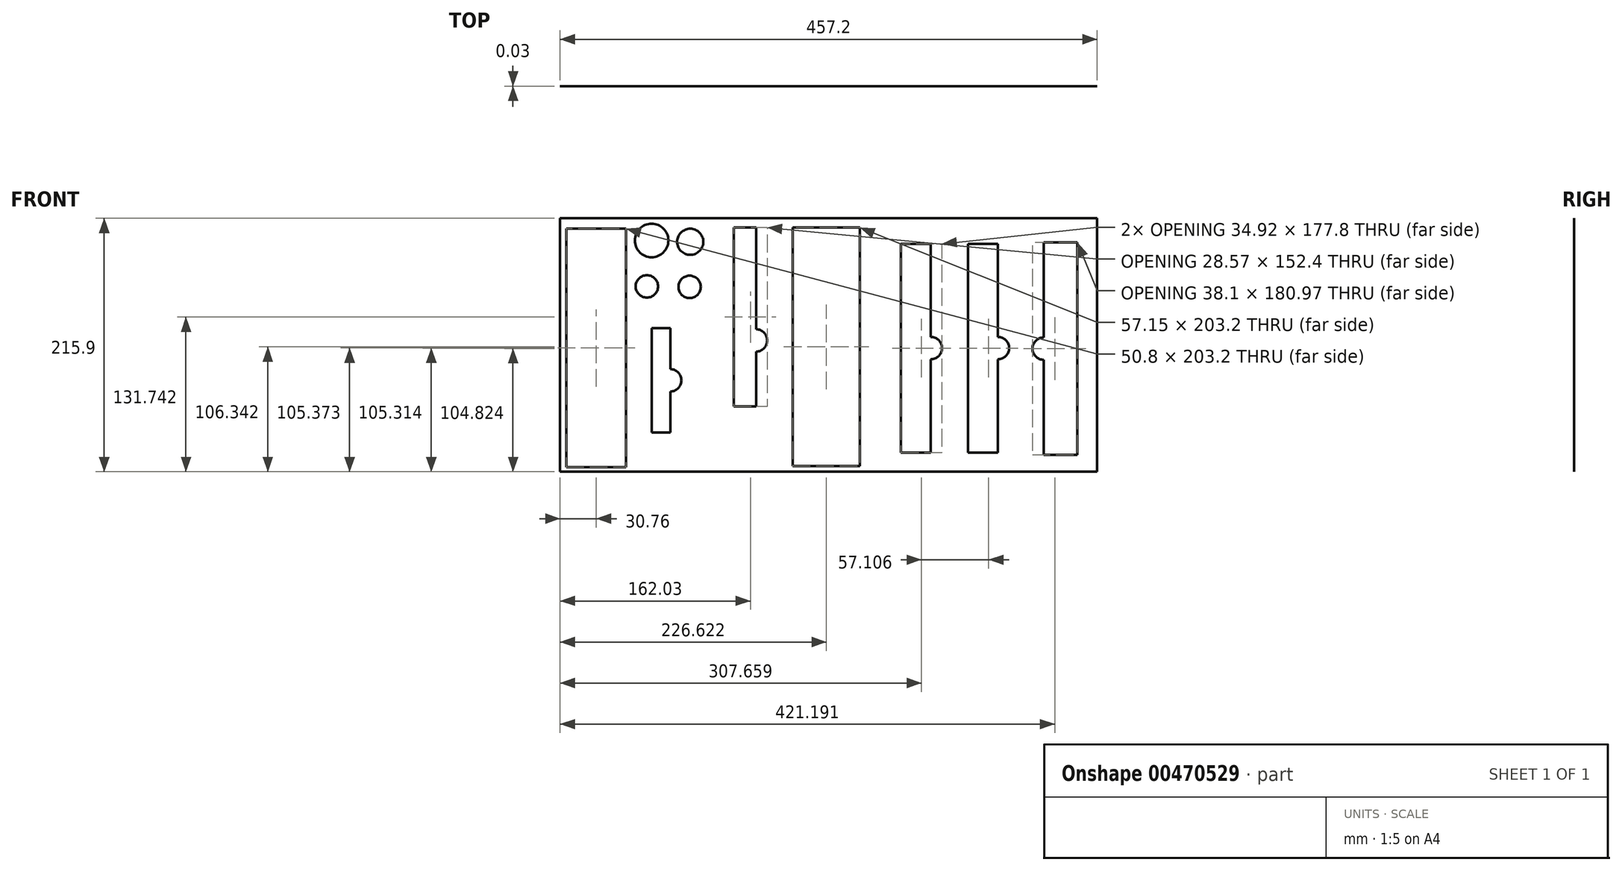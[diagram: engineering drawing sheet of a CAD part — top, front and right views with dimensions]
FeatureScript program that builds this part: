
annotation { "Feature Type Name" : "Feature", "Feature Type Description" : "" }
export const myFeature = defineFeature(function(context is Context, id is Id, definition is map)
    precondition{}
    {
        {
            var Q0;
            Q0=qCreatedBy(makeId("Front.planeOp"),FACE);
            var sketch = newSketch(context, id + "F0", { "sketchPlane" : qUnion([Q0])});
            skLineSegment(sketch, "E0.bottom", {"start": v(-194.02, 115.7) * mm, "end": v(263.18, 115.7) * mm});
            skLineSegment(sketch, "E0.top", {"start": v(-194.02, -100.2) * mm, "end": v(263.18, -100.2) * mm});
            skLineSegment(sketch, "E0.right", {"start": v(263.18, 115.7) * mm, "end": v(263.18, -100.2) * mm});
            skLineSegment(sketch, "E1", {"start": v(-194.02, 115.7) * mm, "end": v(-194.02, -100.2) * mm});
            skSolve(sketch);
        }
        {
            var Q0;
            Q0=makeQuery(id+"F0.imprint","IMPRINT",FACE,{"disambiguationData":[TD([[makeQuery(id+"F0.imprint","IMPRINT",EDGE,{"derivedFrom":sQuery(id+"F0.wireOp",EDGE,"E0.bottom")}),-1.0]])]});
            extrude(context, id + "F1", {"entities" : qUnion([Q0]), "depth" : 3 / 101.6 * mm});
        }
        {
            var Q0;
            Q0=makeQuery(id+"F1.opExtrude","CAP_FACE",FACE,{"disambiguationData":[OSD([sQuery(id+"F0.wireOp",EDGE,"E0.bottom"),sQuery(id+"F0.wireOp",EDGE,"E0.top"),sQuery(id+"F0.wireOp",EDGE,"E0.right"),sQuery(id+"F0.wireOp",EDGE,"E1")])],"isStart":false});
            var sketch = newSketch(context, id + "F2", { "sketchPlane" : qUnion([Q0])});
            skLineSegment(sketch, "E2.bottom", {"start": v(-188.66, 106.77) * mm, "end": v(-137.86, 106.77) * mm});
            skLineSegment(sketch, "E2.top", {"start": v(-188.66, -96.43) * mm, "end": v(-137.86, -96.43) * mm});
            skLineSegment(sketch, "E2.left", {"start": v(-188.66, 106.77) * mm, "end": v(-188.66, -96.43) * mm});
            skLineSegment(sketch, "E2.right", {"start": v(-137.86, 106.77) * mm, "end": v(-137.86, -96.43) * mm});
            skCircle(sketch, "E3", {"center": v(-120.18, 57.68) * mm, "radius": 9.53 * mm});
            skCircle(sketch, "E4", {"center": v(-83.23, 95.66) * mm, "radius": 11.11 * mm});
            skCircle(sketch, "E5", {"center": v(-116.13, 96.76) * mm, "radius": 14.29 * mm});
            skCircle(sketch, "E6", {"center": v(-83.78, 57.22) * mm, "radius": 9.53 * mm});
            skLineSegment(sketch, "E7.bottom", {"start": v(-46.28, 107.74) * mm, "end": v(-27.23, 107.74) * mm});
            skLineSegment(sketch, "E7.top", {"start": v(-46.28, -44.66) * mm, "end": v(-27.23, -44.66) * mm});
            skLineSegment(sketch, "E7.left", {"start": v(-46.28, 107.74) * mm, "end": v(-46.28, -44.66) * mm});
            skLineSegment(sketch, "E7.right", {"start": v(-27.23, 107.74) * mm, "end": v(-27.23, -44.66) * mm});
            skLineSegment(sketch, "E8.bottom", {"start": v(4.03, 107.74) * mm, "end": v(61.18, 107.74) * mm});
            skLineSegment(sketch, "E8.top", {"start": v(4.03, -95.46) * mm, "end": v(61.18, -95.46) * mm});
            skLineSegment(sketch, "E8.left", {"start": v(4.03, 107.74) * mm, "end": v(4.03, -95.46) * mm});
            skLineSegment(sketch, "E8.right", {"start": v(61.18, 107.74) * mm, "end": v(61.18, -95.46) * mm});
            skLineSegment(sketch, "E9.bottom", {"start": v(96.18, 94.01) * mm, "end": v(121.58, 94.01) * mm});
            skLineSegment(sketch, "E9.top", {"start": v(96.18, -83.79) * mm, "end": v(121.58, -83.79) * mm});
            skLineSegment(sketch, "E9.left", {"start": v(96.18, 94.01) * mm, "end": v(96.18, -83.79) * mm});
            skLineSegment(sketch, "E9.right", {"start": v(121.58, 94.01) * mm, "end": v(121.58, -83.79) * mm});
            skLineSegment(sketch, "E10.bottom", {"start": v(153.28, 94.01) * mm, "end": v(178.68, 94.01) * mm});
            skLineSegment(sketch, "E10.top", {"start": v(153.28, -83.79) * mm, "end": v(178.68, -83.79) * mm});
            skLineSegment(sketch, "E10.left", {"start": v(153.28, 94.01) * mm, "end": v(153.28, -83.79) * mm});
            skLineSegment(sketch, "E10.right", {"start": v(178.68, 94.01) * mm, "end": v(178.68, -83.79) * mm});
            skLineSegment(sketch, "E11.bottom", {"start": v(217.65, 95.11) * mm, "end": v(246.22, 95.11) * mm});
            skLineSegment(sketch, "E11.top", {"start": v(217.65, -85.86) * mm, "end": v(246.22, -85.86) * mm});
            skLineSegment(sketch, "E11.left", {"start": v(217.65, 95.11) * mm, "end": v(217.65, -85.86) * mm});
            skLineSegment(sketch, "E11.right", {"start": v(246.22, 95.11) * mm, "end": v(246.22, -85.86) * mm});
            skLineSegment(sketch, "E12.bottom", {"start": v(-116.13, 22.08) * mm, "end": v(-100.26, 22.08) * mm});
            skLineSegment(sketch, "E12.top", {"start": v(-116.13, -66.82) * mm, "end": v(-100.26, -66.82) * mm});
            skLineSegment(sketch, "E12.left", {"start": v(-116.13, 22.08) * mm, "end": v(-116.13, -66.82) * mm});
            skLineSegment(sketch, "E12.right", {"start": v(-100.26, 22.08) * mm, "end": v(-100.26, -66.82) * mm});
            skSolve(sketch);
        }
        {
            var Q0;
            Q0=makeQuery(id+"F2.imprint","IMPRINT",FACE,{"disambiguationData":[TD([[makeQuery(id+"F2.imprint","IMPRINT",EDGE,{"derivedFrom":sQuery(id+"F2.wireOp",EDGE,"E2.bottom")}),-1.0]])]});
            var Q1;
            Q1=makeQuery(id+"F2.imprint","IMPRINT",FACE,{"disambiguationData":[TD([[makeQuery(id+"F2.imprint","IMPRINT",EDGE,{"derivedFrom":sQuery(id+"F2.wireOp",EDGE,"E12.bottom")}),-1.0]])]});
            var Q2;
            Q2=makeQuery(id+"F2.imprint","IMPRINT",FACE,{"disambiguationData":[TD([[makeQuery(id+"F2.imprint","IMPRINT",EDGE,{"derivedFrom":sQuery(id+"F2.wireOp",EDGE,"E7.bottom")}),-1.0]])]});
            var Q3;
            Q3=makeQuery(id+"F2.imprint","IMPRINT",FACE,{"disambiguationData":[TD([[makeQuery(id+"F2.imprint","IMPRINT",EDGE,{"derivedFrom":sQuery(id+"F2.wireOp",EDGE,"E8.bottom")}),-1.0]])]});
            var Q4;
            Q4=makeQuery(id+"F2.imprint","IMPRINT",FACE,{"disambiguationData":[TD([[makeQuery(id+"F2.imprint","IMPRINT",EDGE,{"derivedFrom":sQuery(id+"F2.wireOp",EDGE,"E9.bottom")}),-1.0]])]});
            var Q5;
            Q5=makeQuery(id+"F2.imprint","IMPRINT",FACE,{"disambiguationData":[TD([[makeQuery(id+"F2.imprint","IMPRINT",EDGE,{"derivedFrom":sQuery(id+"F2.wireOp",EDGE,"E10.bottom")}),-1.0]])]});
            var Q6;
            Q6=makeQuery(id+"F2.imprint","IMPRINT",FACE,{"disambiguationData":[TD([[makeQuery(id+"F2.imprint","IMPRINT",EDGE,{"derivedFrom":sQuery(id+"F2.wireOp",EDGE,"E11.bottom")}),-1.0]])]});
            var Q7;
            Q7=makeQuery(id+"F2.imprint","IMPRINT",FACE,{"disambiguationData":[TD([[makeQuery(id+"F2.imprint","IMPRINT",EDGE,{"derivedFrom":sQuery(id+"F2.wireOp",EDGE,"E5")}),1.0]])]});
            var Q8;
            Q8=makeQuery(id+"F2.imprint","IMPRINT",FACE,{"disambiguationData":[TD([[makeQuery(id+"F2.imprint","IMPRINT",EDGE,{"derivedFrom":sQuery(id+"F2.wireOp",EDGE,"E4")}),1.0]])]});
            var Q9;
            Q9=makeQuery(id+"F2.imprint","IMPRINT",FACE,{"disambiguationData":[TD([[makeQuery(id+"F2.imprint","IMPRINT",EDGE,{"derivedFrom":sQuery(id+"F2.wireOp",EDGE,"E6")}),1.0]])]});
            var Q10;
            Q10=makeQuery(id+"F2.imprint","IMPRINT",FACE,{"disambiguationData":[TD([[makeQuery(id+"F2.imprint","IMPRINT",EDGE,{"derivedFrom":sQuery(id+"F2.wireOp",EDGE,"E3")}),1.0]])]});
            extrude(context, id + "F3", {"entities" : qUnion([Q0, Q1, Q2, Q3, Q4, Q5, Q6, Q7, Q8, Q9, Q10]), "operationType" : NewBodyOperationType.REMOVE, "oppositeDirection" : true, "depth" : 7.62 * mm});
        }
        {
            var Q0;
            Q0=makeQuery(id+"F1.opExtrude","CAP_FACE",FACE,{"disambiguationData":[OSD([sQuery(id+"F0.wireOp",EDGE,"E0.bottom"),sQuery(id+"F0.wireOp",EDGE,"E0.top"),sQuery(id+"F0.wireOp",EDGE,"E0.right"),sQuery(id+"F0.wireOp",EDGE,"E1")])],"isStart":false});
            var sketch = newSketch(context, id + "F4", { "sketchPlane" : qUnion([Q0])});
            skCircle(sketch, "E13", {"center": v(178.68, 5.11) * mm, "radius": 9.53 * mm});
            skCircle(sketch, "E14", {"center": v(217.65, 4.62) * mm, "radius": 9.53 * mm});
            skCircle(sketch, "E15", {"center": v(121.58, 5.11) * mm, "radius": 9.53 * mm});
            skCircle(sketch, "E16", {"center": v(-100.26, -22.37) * mm, "radius": 9.53 * mm});
            skCircle(sketch, "E17", {"center": v(-27.23, 11.6) * mm, "radius": 9.53 * mm});
            skSolve(sketch);
        }
        {
            var Q0;
            {var subQ0=sQuery(id+"F4.wireOp",EDGE,"E16");var subQ1=makeQuery(id+"F3.boolean.opBoolean","COPY",EDGE,{"derivedFrom":makeQuery(id+"F3.opExtrude","CAP_EDGE",EDGE,{"disambiguationData":[OSD([sQuery(id+"F2.wireOp",EDGE,"E12.right")])],"isStart":true})});var subQ2=makeQuery(id+"F4.imprint","INTERSECT",VERTEX,{"disambiguationData":[OD(0.0)],"derivedFrom":[subQ1,subQ0]});Q0=makeQuery(id+"F4.imprint","IMPRINT",FACE,{"disambiguationData":[TD([[makeQuery(id+"F4.imprint","IMPRINT",EDGE,{"disambiguationData":[TD([[subQ2,1.0]])],"derivedFrom":subQ0}),1.0]])]});}
            var Q1;
            {var subQ0=sQuery(id+"F4.wireOp",EDGE,"E17");var subQ1=makeQuery(id+"F3.boolean.opBoolean","COPY",EDGE,{"derivedFrom":makeQuery(id+"F3.opExtrude","CAP_EDGE",EDGE,{"disambiguationData":[OSD([sQuery(id+"F2.wireOp",EDGE,"E7.right")])],"isStart":true})});var subQ2=makeQuery(id+"F4.imprint","INTERSECT",VERTEX,{"disambiguationData":[OD(0.0)],"derivedFrom":[subQ1,subQ0]});Q1=makeQuery(id+"F4.imprint","IMPRINT",FACE,{"disambiguationData":[TD([[makeQuery(id+"F4.imprint","IMPRINT",EDGE,{"disambiguationData":[TD([[subQ2,1.0]])],"derivedFrom":subQ0}),1.0]])]});}
            var Q2;
            {var subQ0=sQuery(id+"F4.wireOp",EDGE,"E15");var subQ1=makeQuery(id+"F3.boolean.opBoolean","COPY",EDGE,{"derivedFrom":makeQuery(id+"F3.opExtrude","CAP_EDGE",EDGE,{"disambiguationData":[OSD([sQuery(id+"F2.wireOp",EDGE,"E9.right")])],"isStart":true})});var subQ2=makeQuery(id+"F4.imprint","INTERSECT",VERTEX,{"disambiguationData":[OD(0.0)],"derivedFrom":[subQ1,subQ0]});Q2=makeQuery(id+"F4.imprint","IMPRINT",FACE,{"disambiguationData":[TD([[makeQuery(id+"F4.imprint","IMPRINT",EDGE,{"disambiguationData":[TD([[subQ2,1.0]])],"derivedFrom":subQ0}),1.0]])]});}
            var Q3;
            {var subQ0=sQuery(id+"F4.wireOp",EDGE,"E13");var subQ1=makeQuery(id+"F3.boolean.opBoolean","COPY",EDGE,{"derivedFrom":makeQuery(id+"F3.opExtrude","CAP_EDGE",EDGE,{"disambiguationData":[OSD([sQuery(id+"F2.wireOp",EDGE,"E10.right")])],"isStart":true})});var subQ2=makeQuery(id+"F4.imprint","INTERSECT",VERTEX,{"disambiguationData":[OD(0.0)],"derivedFrom":[subQ1,subQ0]});Q3=makeQuery(id+"F4.imprint","IMPRINT",FACE,{"disambiguationData":[TD([[makeQuery(id+"F4.imprint","IMPRINT",EDGE,{"disambiguationData":[TD([[subQ2,1.0]])],"derivedFrom":subQ0}),1.0]])]});}
            var Q4;
            {var subQ0=sQuery(id+"F4.wireOp",EDGE,"E14");var subQ1=makeQuery(id+"F3.boolean.opBoolean","COPY",EDGE,{"derivedFrom":makeQuery(id+"F3.opExtrude","CAP_EDGE",EDGE,{"disambiguationData":[OSD([sQuery(id+"F2.wireOp",EDGE,"E11.left")])],"isStart":true})});var subQ2=makeQuery(id+"F4.imprint","INTERSECT",VERTEX,{"disambiguationData":[OD(0.0)],"derivedFrom":[subQ1,subQ0]});Q4=makeQuery(id+"F4.imprint","IMPRINT",FACE,{"disambiguationData":[TD([[makeQuery(id+"F4.imprint","IMPRINT",EDGE,{"disambiguationData":[TD([[subQ2,1.0]])],"derivedFrom":subQ0}),1.0]])]});}
            var Q5;
            {var subQ0=sQuery(id+"F4.wireOp",EDGE,"E14");var subQ1=makeQuery(id+"F3.boolean.opBoolean","COPY",EDGE,{"derivedFrom":makeQuery(id+"F3.opExtrude","CAP_EDGE",EDGE,{"disambiguationData":[OSD([sQuery(id+"F2.wireOp",EDGE,"E11.left")])],"isStart":true})});var subQ2=makeQuery(id+"F4.imprint","INTERSECT",VERTEX,{"disambiguationData":[OD(0.0)],"derivedFrom":[subQ1,subQ0]});Q5=makeQuery(id+"F4.imprint","IMPRINT",FACE,{"disambiguationData":[TD([[makeQuery(id+"F4.imprint","IMPRINT",EDGE,{"disambiguationData":[TD([[subQ2,-1.0]])],"derivedFrom":subQ0}),1.0]])]});}
            extrude(context, id + "F5", {"entities" : qUnion([Q0, Q1, Q2, Q3, Q4, Q5]), "operationType" : NewBodyOperationType.REMOVE, "oppositeDirection" : true, "depth" : 7.62 * mm});
        }
    });
